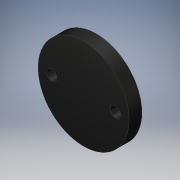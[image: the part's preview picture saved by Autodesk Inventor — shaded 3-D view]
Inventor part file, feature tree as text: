
AUTODESK INVENTOR PART (.ipt)
format: ipt  version: 2019.4 (Build 234330000, 330)  size: 107,008 bytes
history: native  units: mm
features: extrude x1, sketch x1
ambient origin geometry x8: Origin, YZ Plane, XZ Plane, XY Plane, X Axis, Y Axis, Z Axis, Center Point
bodies: Solid1 (feature_tree)
feature tree (2):
  extrude  "Extrusion1"  Depth=3.1mm
  sketch  "Sketch1"  dims[d0=22.0mm d1=15.4mm d2=2.5mm d3=2.5mm d4=3.1mm d5=0.0mm]
